# Revit family: Zumtobel SUPERSYSTEM II M1
name_source: partatom
category: Lighting Fixtures
revit_build: Autodesk Revit 2016 (Build: 20150220_1215(x64)
units: mm (PartAtom-declared; Revit-internal decimal feet)

## family parameters
Cut with Voids When Loaded = No
Host = Face
Light Source = No
OmniClass Number = 23.80.70.11
OmniClass Title = Luminaries for Internal Lighting
Part Type = Normal
Room Calculation Point = No
Round Connector Dimension = Use Diameter
Shared = No

## types (1)
- SUP2 M 1/LED550-940 WFL LDO WH
    Apparent Load = 0 VA
    Assembly Code = D5020200
    Body = Zumtobel_Metal_White
    Default Elevation = 0 mm  [stored 0 ft]
    Description = LED spot luminaires
    Height = 74 mm  [stored 0.242782 ft]
    Lamp = LED
    Length = 166 mm  [stored 0.544619 ft]
    Manufacturer = Zumtobel Lighting
    Model = 42927632
    Reflector = Zumtobel_Cover_Self_llumination_Opaque
    URL = http://www.zumtobel.com
    Voltage = 230 V

note: [stored X ft] marks values corroborated as IEEE doubles in the binary element streams (Revit-internal decimal feet)

## geometry (parser evidence)
native form markers: Sweep x8
no freeform markers — native parametric forms only
